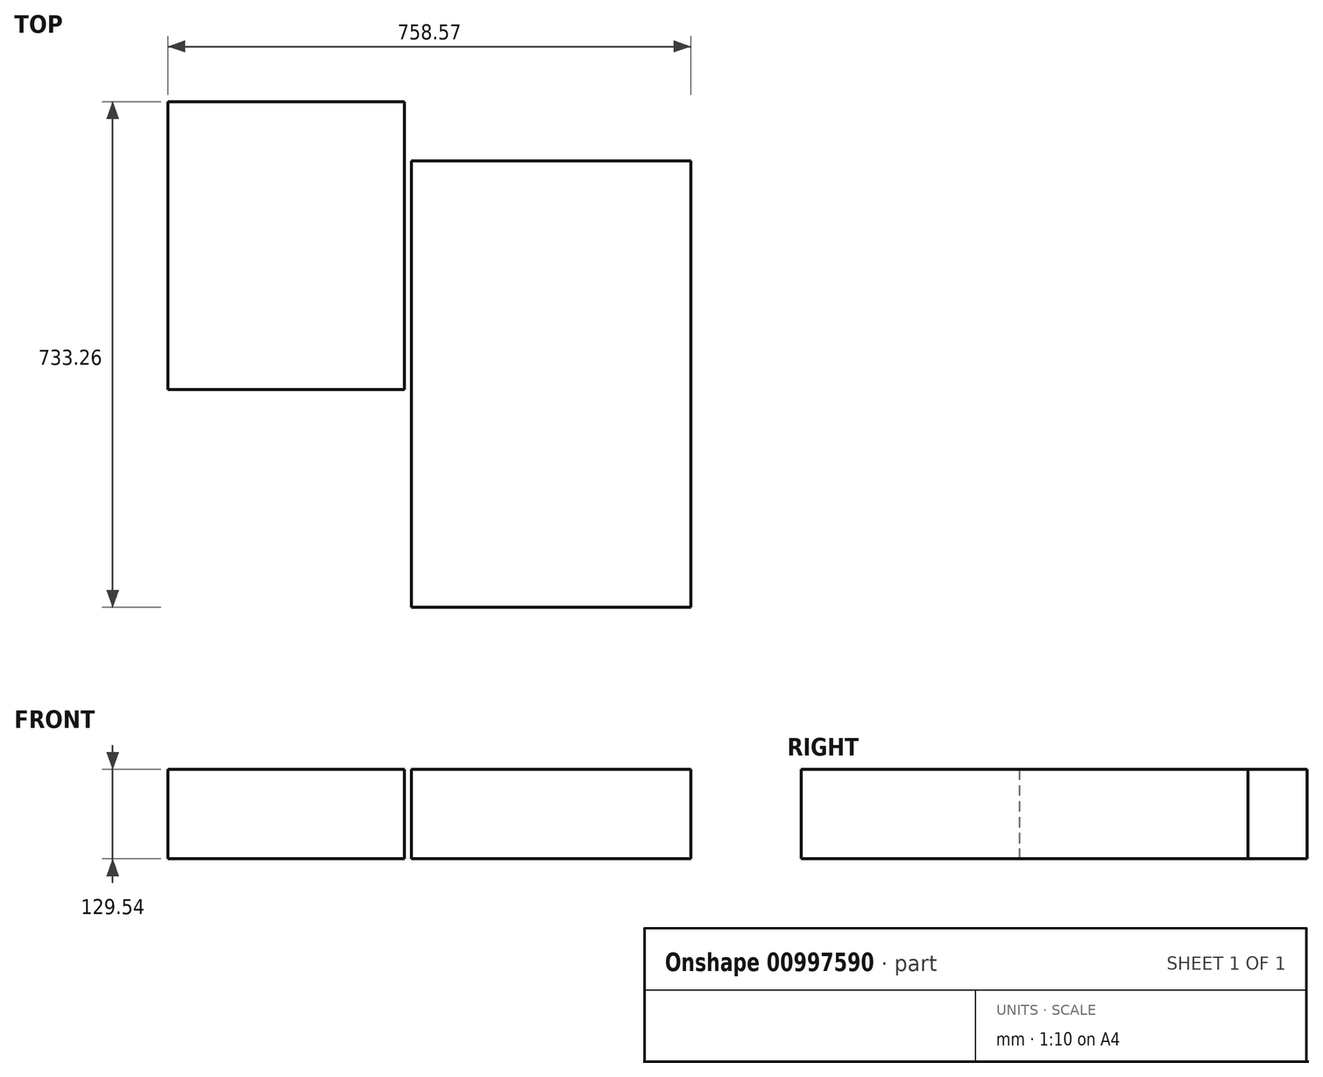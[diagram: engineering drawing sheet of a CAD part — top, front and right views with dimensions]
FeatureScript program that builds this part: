
annotation { "Feature Type Name" : "Feature", "Feature Type Description" : "" }
export const myFeature = defineFeature(function(context is Context, id is Id, definition is map)
    precondition{}
    {
        {
            var Q0;
            Q0=qCreatedBy(makeId("Top.planeOp"),FACE);
            var sketch = newSketch(context, id + "F0", { "sketchPlane" : qUnion([Q0])});
            skLineSegment(sketch, "E0.bottom", {"start": v(32.38, 7.28) * mm, "end": v(437.94, 7.28) * mm});
            skLineSegment(sketch, "E0.top", {"start": v(32.38, -639.92) * mm, "end": v(437.94, -639.92) * mm});
            skLineSegment(sketch, "E0.left", {"start": v(32.38, 7.28) * mm, "end": v(32.38, -639.92) * mm});
            skLineSegment(sketch, "E0.right", {"start": v(437.94, 7.28) * mm, "end": v(437.94, -639.92) * mm});
            skLineSegment(sketch, "E1.bottom", {"start": v(22.57, 93.34) * mm, "end": v(-320.63, 93.34) * mm});
            skLineSegment(sketch, "E1.top", {"start": v(22.57, -324.15) * mm, "end": v(-320.63, -324.15) * mm});
            skLineSegment(sketch, "E1.left", {"start": v(22.57, 93.34) * mm, "end": v(22.57, -324.15) * mm});
            skLineSegment(sketch, "E1.right", {"start": v(-320.63, 93.34) * mm, "end": v(-320.63, -324.15) * mm});
            skSolve(sketch);
        }
        {
            var Q0;
            Q0=makeQuery(id+"F0.imprint","IMPRINT",FACE,{"disambiguationData":[TD([[makeQuery(id+"F0.imprint","IMPRINT",EDGE,{"derivedFrom":sQuery(id+"F0.wireOp",EDGE,"E1.bottom")}),1.0]])]});
            var Q1;
            Q1=makeQuery(id+"F0.imprint","IMPRINT",FACE,{"disambiguationData":[TD([[makeQuery(id+"F0.imprint","IMPRINT",EDGE,{"derivedFrom":sQuery(id+"F0.wireOp",EDGE,"E0.bottom")}),-1.0]])]});
            extrude(context, id + "F1", {"entities" : qUnion([Q0, Q1]), "depth" : 129.54 * mm, "offsetDistance" : 25.4 * mm});
        }
    });
